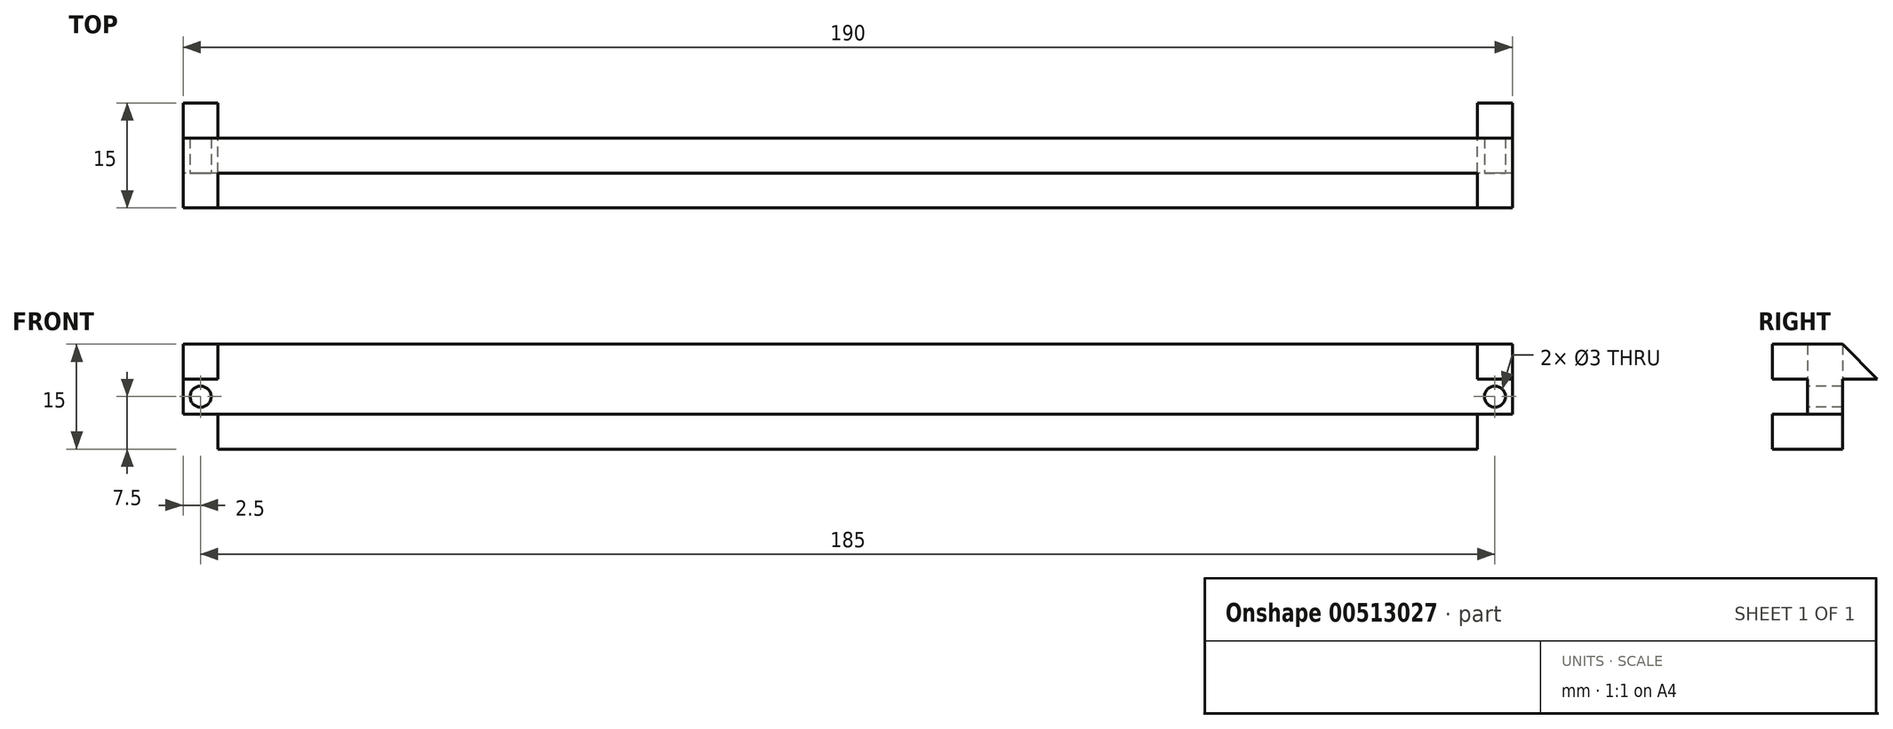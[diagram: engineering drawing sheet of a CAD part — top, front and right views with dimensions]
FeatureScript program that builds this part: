
annotation { "Feature Type Name" : "Feature", "Feature Type Description" : "" }
export const myFeature = defineFeature(function(context is Context, id is Id, definition is map)
    precondition{}
    {
        {
            var Q0;
            Q0=qCreatedBy(makeId("Top.planeOp"),FACE);
            var sketch = newSketch(context, id + "F0", { "sketchPlane" : qUnion([Q0])});
            skLineSegment(sketch, "E0.bottom", {"start": v(90, -5) * mm, "end": v(-90, -5) * mm});
            skLineSegment(sketch, "E0.top", {"start": v(90, 5) * mm, "end": v(-90, 5) * mm});
            skLineSegment(sketch, "E0.left", {"start": v(90, -5) * mm, "end": v(90, 5) * mm});
            skLineSegment(sketch, "E0.right", {"start": v(-90, -5) * mm, "end": v(-90, 5) * mm});
            skPoint(sketch, "E0.middle", {"position": v(0, 0) * mm});
            skSolve(sketch);
        }
        {
            var Q0;
            Q0 = qSketchRegion(id + "F0", true);
            extrude(context, id + "F1", {"entities" : qUnion([Q0]), "depth" : 15 * mm});
        }
        {
            var Q0;
            Q0=makeQuery(id+"F1.opExtrude","SWEPT_FACE",FACE,{"disambiguationData":[OSD([sQuery(id+"F0.wireOp",EDGE,"E0.bottom")])]});
            var sketch = newSketch(context, id + "F2", { "sketchPlane" : qUnion([Q0])});
            skLineSegment(sketch, "E1.bottom", {"start": v(-90, 15) * mm, "end": v(90, 15) * mm});
            skLineSegment(sketch, "E1.top", {"start": v(-90, 5) * mm, "end": v(90, 5) * mm});
            skLineSegment(sketch, "E1.left", {"start": v(-90, 15) * mm, "end": v(-90, 5) * mm});
            skLineSegment(sketch, "E1.right", {"start": v(90, 15) * mm, "end": v(90, 5) * mm});
            skSolve(sketch);
        }
        {
            var Q0;
            Q0 = qSketchRegion(id + "F2", true);
            extrude(context, id + "F3", {"entities" : qUnion([Q0]), "operationType" : NewBodyOperationType.REMOVE, "oppositeDirection" : true, "depth" : 5 * mm});
        }
        {
            var Q0;
            Q0=makeQuery(id+"F1.opExtrude","SWEPT_FACE",FACE,{"disambiguationData":[OSD([sQuery(id+"F0.wireOp",EDGE,"E0.right")])]});
            var sketch = newSketch(context, id + "F4", { "sketchPlane" : qUnion([Q0])});
            skLineSegment(sketch, "E2.bottom", {"start": v(0, 15) * mm, "end": v(-5, 15) * mm});
            skLineSegment(sketch, "E2.top", {"start": v(0, 5) * mm, "end": v(-5, 5) * mm});
            skLineSegment(sketch, "E2.left", {"start": v(0, 15) * mm, "end": v(0, 5) * mm});
            skLineSegment(sketch, "E2.right", {"start": v(-5, 15) * mm, "end": v(-5, 5) * mm});
            skSolve(sketch);
        }
        {
            var Q0;
            Q0 = qSketchRegion(id + "F4", true);
            extrude(context, id + "F5", {"entities" : qUnion([Q0]), "operationType" : NewBodyOperationType.ADD, "depth" : 5 * mm});
        }
        {
            var Q0;
            Q0=makeQuery(id+"F5.boolean.opBoolean","MERGE",FACE,{"derivedFrom":[makeQuery(id+"F3.boolean.opBoolean","COPY",FACE,{"derivedFrom":makeQuery(id+"F3.opExtrude","CAP_FACE",FACE,{"disambiguationData":[OSD([sQuery(id+"F2.wireOp",EDGE,"E1.bottom"),sQuery(id+"F2.wireOp",EDGE,"E1.top"),sQuery(id+"F2.wireOp",EDGE,"E1.left"),sQuery(id+"F2.wireOp",EDGE,"E1.right")])],"isStart":false})}),makeQuery(id+"F5.opExtrude","SWEPT_FACE",FACE,{"disambiguationData":[OSD([sQuery(id+"F4.wireOp",EDGE,"E2.left")])]})]});
            var sketch = newSketch(context, id + "F6", { "sketchPlane" : qUnion([Q0])});
            skLineSegment(sketch, "E3.bottom", {"start": v(-90, 5) * mm, "end": v(-95, 5) * mm});
            skLineSegment(sketch, "E3.top", {"start": v(-90, 10) * mm, "end": v(-95, 10) * mm});
            skLineSegment(sketch, "E3.left", {"start": v(-90, 5) * mm, "end": v(-90, 10) * mm});
            skLineSegment(sketch, "E3.right", {"start": v(-95, 5) * mm, "end": v(-95, 10) * mm});
            skCircle(sketch, "E4", {"center": v(-92.5, 7.5) * mm, "radius": 1.5 * mm});
            skPoint(sketch, "E4.centerSnap0", {"position": v(-95, 7.5) * mm});
            skPoint(sketch, "E4.centerSnap1", {"position": v(-92.5, 10) * mm});
            skSolve(sketch);
        }
        {
            var Q0;
            Q0=makeQuery(id+"F6.imprint","IMPRINT",FACE,{"disambiguationData":[TD([[makeQuery(id+"F6.imprint","IMPRINT",EDGE,{"derivedFrom":sQuery(id+"F6.wireOp",EDGE,"E4")}),1.0]])]});
            extrude(context, id + "F7", {"entities" : qUnion([Q0]), "operationType" : NewBodyOperationType.REMOVE, "oppositeDirection" : true, "depth" : 25 * mm});
        }
        {
            var Q0;
            Q0=makeQuery(id+"F1.opExtrude","CAP_FACE",FACE,{"disambiguationData":[OSD([sQuery(id+"F0.wireOp",EDGE,"E0.bottom"),sQuery(id+"F0.wireOp",EDGE,"E0.top"),sQuery(id+"F0.wireOp",EDGE,"E0.left"),sQuery(id+"F0.wireOp",EDGE,"E0.right")])],"isStart":true});
            var sketch = newSketch(context, id + "F8", { "sketchPlane" : qUnion([Q0])});
            skLineSegment(sketch, "E5", {"start": v(0, -5) * mm, "end": v(0, 5) * mm});
            skSolve(sketch);
        }
        {
            var Q0;
            {var subQ0=sQuery(id+"F8.wireOp",EDGE,"E5");Q0=makeQuery(id+"F8.imprint","IMPRINT",FACE,{"disambiguationData":[TD([[makeQuery(id+"F8.imprint","IMPRINT",EDGE,{"derivedFrom":subQ0}),-1.0]])]});}
            extrude(context, id + "F9", {"entities" : qUnion([Q0]), "operationType" : NewBodyOperationType.REMOVE, "oppositeDirection" : true, "depth" : 25 * mm});
        }
        {
            var Q0;
            Q0=makeQuery(id+"F5.opExtrude","CAP_FACE",FACE,{"disambiguationData":[OSD([sQuery(id+"F4.wireOp",EDGE,"E2.bottom"),sQuery(id+"F4.wireOp",EDGE,"E2.top"),sQuery(id+"F4.wireOp",EDGE,"E2.left"),sQuery(id+"F4.wireOp",EDGE,"E2.right")])],"isStart":false});
            var sketch = newSketch(context, id + "F10", { "sketchPlane" : qUnion([Q0])});
            skLineSegment(sketch, "E6.bottom", {"start": v(-5, 15) * mm, "end": v(0, 15) * mm});
            skLineSegment(sketch, "E6.top", {"start": v(-5, 10) * mm, "end": v(0, 10) * mm});
            skLineSegment(sketch, "E6.left", {"start": v(-5, 15) * mm, "end": v(-5, 10) * mm});
            skLineSegment(sketch, "E6.right", {"start": v(0, 15) * mm, "end": v(0, 10) * mm});
            skLineSegment(sketch, "E7", {"start": v(-5, 10) * mm, "end": v(-10, 10) * mm});
            skLineSegment(sketch, "E8", {"start": v(-10, 10) * mm, "end": v(-5, 15) * mm});
            skLineSegment(sketch, "E9", {"start": v(0, 10) * mm, "end": v(5, 10) * mm});
            skLineSegment(sketch, "E10", {"start": v(5, 10) * mm, "end": v(5, 15) * mm});
            skLineSegment(sketch, "E11", {"start": v(5, 15) * mm, "end": v(0, 15) * mm});
            skSolve(sketch);
        }
        {
            var Q0;
            Q0=makeQuery(id+"F10.imprint","IMPRINT",FACE,{"disambiguationData":[TD([[makeQuery(id+"F10.imprint","IMPRINT",EDGE,{"derivedFrom":sQuery(id+"F10.wireOp",EDGE,"E6.left")}),-1.0]])]});
            var Q1;
            Q1=makeQuery(id+"F10.imprint","IMPRINT",FACE,{"disambiguationData":[TD([[makeQuery(id+"F10.imprint","IMPRINT",EDGE,{"derivedFrom":sQuery(id+"F10.wireOp",EDGE,"E6.right")}),1.0]])]});
            extrude(context, id + "F11", {"entities" : qUnion([Q0, Q1]), "operationType" : NewBodyOperationType.ADD, "oppositeDirection" : true, "depth" : 5 * mm});
        }
        {
            var Q0;
            Q0=makeQuery(id+"F1.opExtrude","SWEPT_BODY",BODY,{"disambiguationData":[OSD([sQuery(id+"F0.wireOp",EDGE,"E0.bottom"),sQuery(id+"F0.wireOp",EDGE,"E0.top"),sQuery(id+"F0.wireOp",EDGE,"E0.left"),sQuery(id+"F0.wireOp",EDGE,"E0.right")])]});
            var Q1;
            Q1=makeQuery(id+"F9.boolean.opBoolean","COPY",FACE,{"derivedFrom":makeQuery(id+"F9.opExtrude","SWEPT_FACE",FACE,{"disambiguationData":[OSD([sQuery(id+"F8.wireOp",EDGE,"E5")])]})});
            mirror(context, id + "F12", {"operationType" : NewBodyOperationType.ADD, "entities" : qUnion([Q0]), "mirrorPlane" : qUnion([Q1])});
        }
    });
